# Revit family: Neptun Magna
name_source: partatom
category: HLS-Bauteile
units: mm (PartAtom-declared; Revit-internal decimal feet)

## family parameters
Arbeitsebenenbasiert = Nein
Beim Laden mit Abzugskörper schneiden = Nein
Bemaßung runder Anschluss = Durchmesser verwenden
Beschriftungsausrichtung beibehalten = Nein
Gemeinsam genutzt = Nein
Immer vertikal = Ja
Klassifizierung = Keine
Raumberechnungspunkt = Nein
Teiletyp = Normal

## types (6) — shared parameters
Anschluss 1 1/2" = 40 mm  [stored 0.131234 ft]
Anschluss 3/4" = 20 mm  [stored 0.0656168 ft]
Behälterkopf = 150 mm  [stored 0.492126 ft]
Datenblatt = https://www.burkhalter-h2o.ch
Homepage = https://www.burkhalter-h2o.ch
LUT = LUT_Neptun_Magna
Sockel_Höhe = 100 mm  [stored 0.328084 ft]
Steuerung_Breite = 200 mm  [stored 0.656168 ft]
Steuerung_Höhe = 225 mm  [stored 0.738189 ft]
Steuerung_Tiefe = 75 mm  [stored 0.246063 ft]
zero-valued in all types: Vorgabe-Ansicht

## per-type parameters (varying)
| type | A | B | C | Harzinhalt_pro_Harzdruckbehälter | Sockel_Absatz_Oben | Sockel_Absatz_Unten |
| Neptun Magna - 50L | 305 mm  [stored 1.00066 ft] | 1460 mm  [stored 4.79003 ft] | 1315 mm  [stored 4.3143 ft] | 50L | 133 mm | 163 mm |
| Neptun Magna - 75L | 369 mm  [stored 1.21063 ft] | 1900 mm  [stored 6.2336 ft] | 1755 mm  [stored 5.75787 ft] | 75L | 165 mm | 195 mm |
| Neptun Magna - 100L | 406 mm  [stored 1.33202 ft] | 1900 mm  [stored 6.2336 ft] | 1755 mm  [stored 5.75787 ft] | 100L | 183 mm | 213 mm  [stored 0.698819 ft] |
| Neptun Magna - 125L | 406 mm  [stored 1.33202 ft] | 1900 mm  [stored 6.2336 ft] | 1755 mm  [stored 5.75787 ft] | 125L | 183 mm | 213 mm  [stored 0.698819 ft] |
| Neptun Magna - 150L | 552 mm  [stored 1.81102 ft] | 1860 mm  [stored 6.10236 ft] | 1715 mm  [stored 5.62664 ft] | 150L | 256 mm  [stored 0.839895 ft] | 286 mm |
| Neptun Magna - 200L | 552 mm  [stored 1.81102 ft] | 1860 mm  [stored 6.10236 ft] | 1715 mm  [stored 5.62664 ft] | 200L | 256 mm  [stored 0.839895 ft] | 286 mm |

note: [stored X ft] marks values corroborated as IEEE doubles in the binary element streams (Revit-internal decimal feet)
